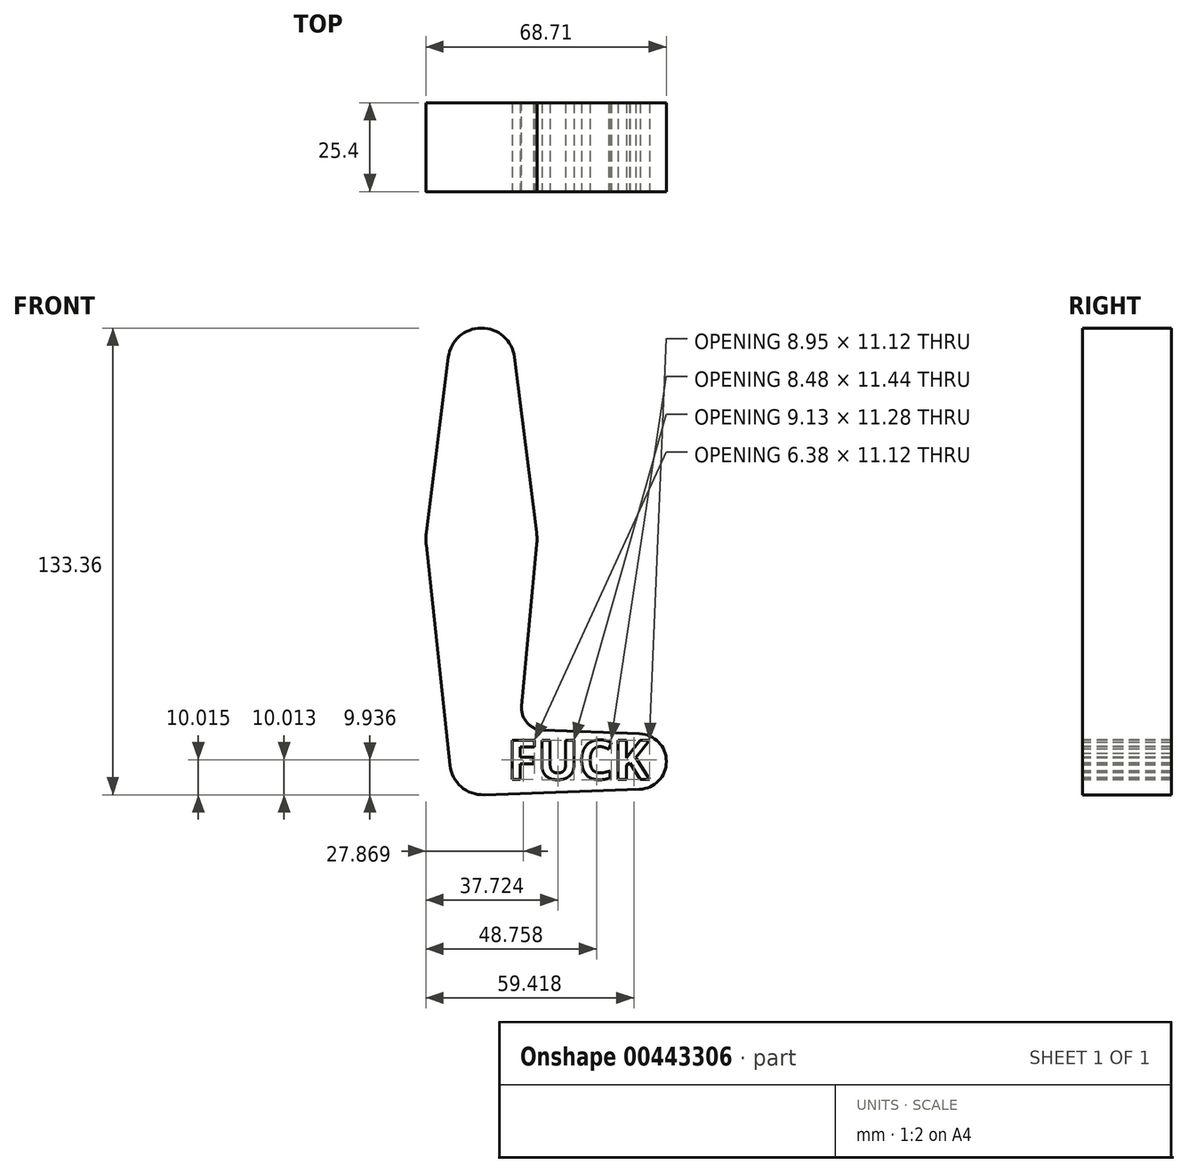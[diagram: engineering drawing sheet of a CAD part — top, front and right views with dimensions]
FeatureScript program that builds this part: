
annotation { "Feature Type Name" : "Feature", "Feature Type Description" : "" }
export const myFeature = defineFeature(function(context is Context, id is Id, definition is map)
    precondition{}
    {
        {
            var Q0;
            Q0=qCreatedBy(makeId("Front.planeOp"),FACE);
            var sketch = newSketch(context, id + "F0", { "sketchPlane" : qUnion([Q0])});
            skCircle(sketch, "E0", {"center": v(0, 0) * mm, "radius": 15.88 * mm});
            skCircle(sketch, "E1", {"center": v(0, 50.8) * mm, "radius": 9.53 * mm});
            skLineSegment(sketch, "E2", {"start": v(-9.45, 52) * mm, "end": v(-15.75, 1.98) * mm});
            skLineSegment(sketch, "E3", {"start": v(9.45, 52) * mm, "end": v(15.75, 1.98) * mm});
            skArc(sketch, "E4.MirrorC", {"start": v(0.78, -73.02) * mm, "mid": v(-5.8, -70.7) * mm, "end": v(-9.03, -64.52) * mm});
            skCircle(sketch, "E5", {"center": v(44.89, -63.5) * mm, "radius": 7.94 * mm});
            skLineSegment(sketch, "E6", {"start": v(17.58, -54.58) * mm, "end": v(45.17, -55.57) * mm});
            skLineSegment(sketch, "E7", {"start": v(45.17, -71.43) * mm, "end": v(0.78, -73.02) * mm});
            skLineSegment(sketch, "E8", {"start": v(-9.03, -64.52) * mm, "end": v(-15.78, -1.7) * mm});
            skLineSegment(sketch, "E9.trimOffspring", {"start": v(11.49, -47.64) * mm, "end": v(15.8, -1.48) * mm});
            skPoint(sketch, "E10.visualSharp", {"position": v(10.86, -54.34) * mm});
            skArc(sketch, "E10.filletArc", {"start": v(11.49, -47.64) * mm, "mid": v(13.04, -52.43) * mm, "end": v(17.58, -54.58) * mm});
            skSolve(sketch);
        }
        {
            var Q0;
            Q0 = qSketchRegion(id + "F0", true);
            extrude(context, id + "F1", {"entities" : qUnion([Q0]), "depth" : 25.4 * mm});
        }
        {
            var Q0;
            Q0=makeQuery(id+"F1.opExtrude","CAP_FACE",FACE,{"disambiguationData":[OSD([sQuery(id+"F0.wireOp",EDGE,"E0"),sQuery(id+"F0.wireOp",EDGE,"E1"),sQuery(id+"F0.wireOp",EDGE,"E2"),sQuery(id+"F0.wireOp",EDGE,"E3"),sQuery(id+"F0.wireOp",EDGE,"E4.MirrorC"),sQuery(id+"F0.wireOp",EDGE,"E5"),sQuery(id+"F0.wireOp",EDGE,"E6"),sQuery(id+"F0.wireOp",EDGE,"E7"),sQuery(id+"F0.wireOp",EDGE,"E8"),sQuery(id+"F0.wireOp",EDGE,"E9.trimOffspring"),sQuery(id+"F0.wireOp",EDGE,"E10.filletArc")])],"isStart":false});
            var sketch = newSketch(context, id + "F2", { "sketchPlane" : qUnion([Q0])});
            skText(sketch, "E11", { "text": "FUCK", "fontName": "OpenSans-Bold.ttf"});
            const initialGuessF2  = {"E11": [0.0074, -0.06858, 1, 0, 0.01122]};
            skSetInitialGuess(sketch, initialGuessF2);
            skSolve(sketch);
        }
        {
            var Q0;
            Q0 = qSketchRegion(id + "F2", true);
            extrude(context, id + "F3", {"entities" : qUnion([Q0]), "operationType" : NewBodyOperationType.REMOVE, "oppositeDirection" : true, "depth" : 25.4 * mm});
        }
    });
